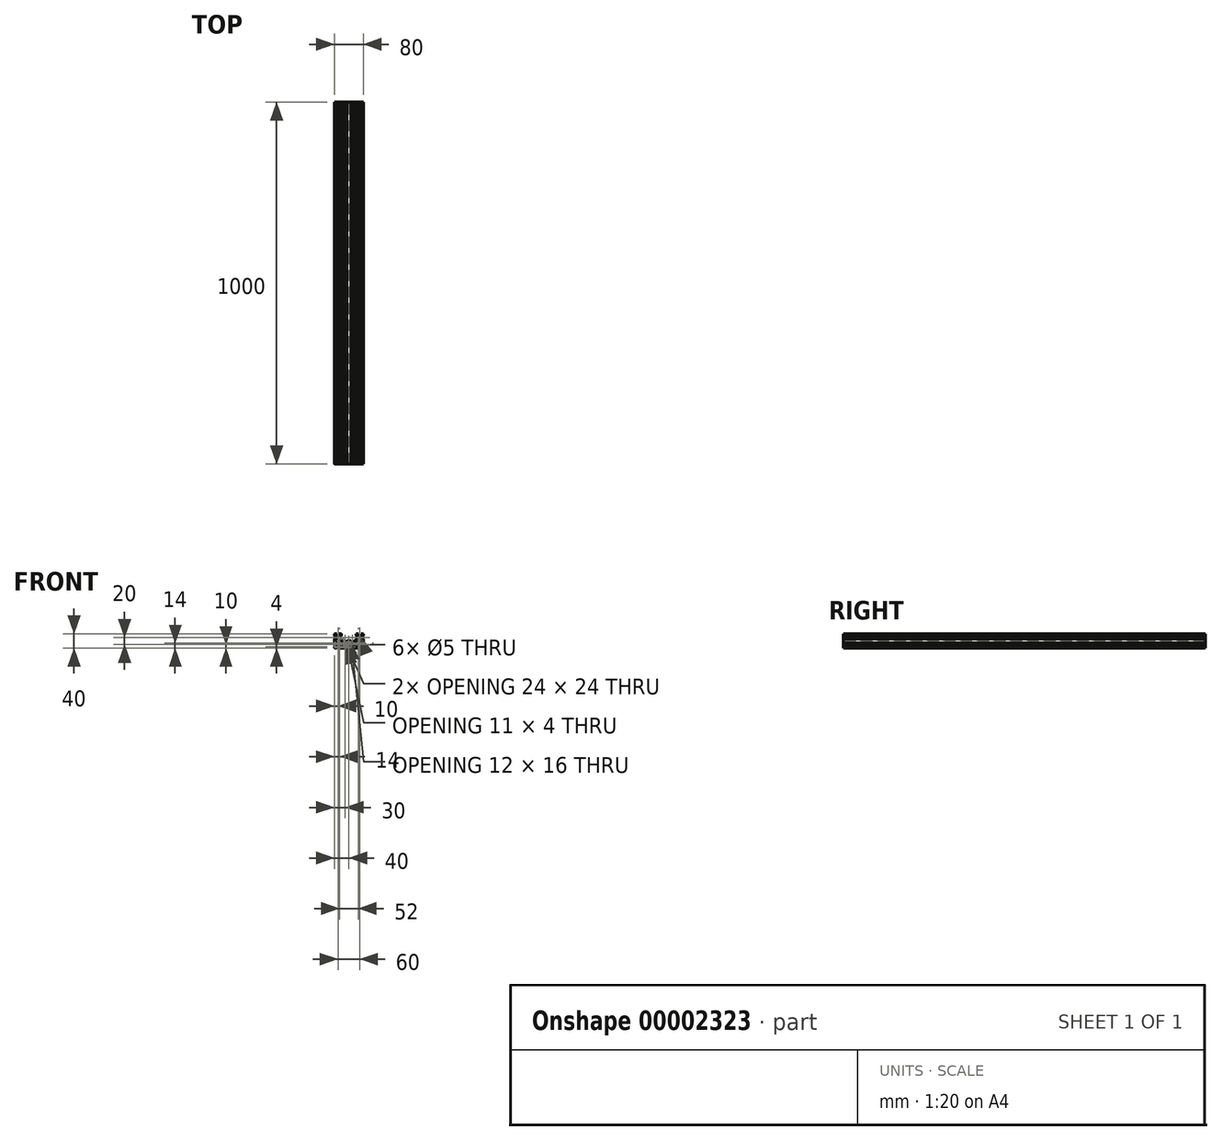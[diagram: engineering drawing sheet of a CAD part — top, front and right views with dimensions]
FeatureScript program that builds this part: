
annotation { "Feature Type Name" : "Feature", "Feature Type Description" : "" }
export const myFeature = defineFeature(function(context is Context, id is Id, definition is map)
    precondition{}
    {
        {
            var Q0;
            Q0=qCreatedBy(makeId("Front.planeOp"),FACE);
            var sketch = newSketch(context, id + "F0", { "sketchPlane" : qUnion([Q0])});
            skLineSegment(sketch, "E0", {"start": v(0, 0) * mm, "end": v(0, 40) * mm});
            skLineSegment(sketch, "E1", {"start": v(0, 40) * mm, "end": v(20, 40) * mm});
            skLineSegment(sketch, "E2", {"start": v(20, 40) * mm, "end": v(20, 20) * mm});
            skLineSegment(sketch, "E3", {"start": v(20, 20) * mm, "end": v(60, 20) * mm});
            skLineSegment(sketch, "E4", {"start": v(60, 20) * mm, "end": v(60, 40) * mm});
            skLineSegment(sketch, "E5", {"start": v(60, 40) * mm, "end": v(80, 40) * mm});
            skLineSegment(sketch, "E6", {"start": v(80, 40) * mm, "end": v(80, 0) * mm});
            skLineSegment(sketch, "E7", {"start": v(80, 0) * mm, "end": v(0, 0) * mm});
            skCircle(sketch, "E8", {"center": v(10, 30) * mm, "radius": 2.5 * mm});
            skCircle(sketch, "E9", {"center": v(10, 10) * mm, "radius": 2.5 * mm});
            skCircle(sketch, "E10", {"center": v(30, 10) * mm, "radius": 2.5 * mm});
            skCircle(sketch, "E11", {"center": v(50, 10) * mm, "radius": 2.5 * mm});
            skCircle(sketch, "E12", {"center": v(70, 10) * mm, "radius": 2.5 * mm});
            skCircle(sketch, "E13", {"center": v(70, 30) * mm, "radius": 2.5 * mm});
            skLineSegment(sketch, "E14.0", {"start": v(2, 4) * mm, "end": v(2, 15) * mm});
            skLineSegment(sketch, "E14.1", {"start": v(76, 2) * mm, "end": v(65, 2) * mm});
            skLineSegment(sketch, "E14.2", {"start": v(78, 36) * mm, "end": v(78, 25) * mm});
            skLineSegment(sketch, "E14.3", {"start": v(64, 38) * mm, "end": v(76, 38) * mm});
            skLineSegment(sketch, "E14.4", {"start": v(62, 18) * mm, "end": v(62, 23) * mm});
            skLineSegment(sketch, "E14.5", {"start": v(4, 38) * mm, "end": v(16, 38) * mm});
            skLineSegment(sketch, "E14.6", {"start": v(18, 18) * mm, "end": v(22.5, 18) * mm});
            skLineSegment(sketch, "E14.7", {"start": v(18, 36) * mm, "end": v(18, 25) * mm});
            skLineSegment(sketch, "E15.bottom", {"start": v(0, 40) * mm, "end": v(4, 40) * mm});
            skLineSegment(sketch, "E15.top", {"start": v(2, 36) * mm, "end": v(2.59, 36) * mm});
            skLineSegment(sketch, "E15.left", {"start": v(0, 40) * mm, "end": v(0, 36) * mm});
            skLineSegment(sketch, "E15.right", {"start": v(4, 38) * mm, "end": v(4, 37.41) * mm});
            skLineSegment(sketch, "E16.bottom", {"start": v(20, 40) * mm, "end": v(16, 40) * mm});
            skLineSegment(sketch, "E16.top", {"start": v(18, 36) * mm, "end": v(17.41, 36) * mm});
            skLineSegment(sketch, "E16.left", {"start": v(20, 40) * mm, "end": v(20, 36) * mm});
            skLineSegment(sketch, "E16.right", {"start": v(16, 38) * mm, "end": v(16, 37.41) * mm});
            skLineSegment(sketch, "E17.bottom", {"start": v(0, 0) * mm, "end": v(4, 0) * mm});
            skLineSegment(sketch, "E17.top", {"start": v(2, 4) * mm, "end": v(2.59, 4) * mm});
            skLineSegment(sketch, "E17.left", {"start": v(0, 0) * mm, "end": v(0, 4) * mm});
            skLineSegment(sketch, "E17.right", {"start": v(4, 2) * mm, "end": v(4, 2.59) * mm});
            skLineSegment(sketch, "E18.bottom", {"start": v(60, 40) * mm, "end": v(64, 40) * mm});
            skLineSegment(sketch, "E18.top", {"start": v(62, 36) * mm, "end": v(62.59, 36) * mm});
            skLineSegment(sketch, "E18.left", {"start": v(60, 40) * mm, "end": v(60, 36) * mm});
            skLineSegment(sketch, "E18.right", {"start": v(64, 38) * mm, "end": v(64, 37.41) * mm});
            skLineSegment(sketch, "E19.bottom", {"start": v(80, 40) * mm, "end": v(76, 40) * mm});
            skLineSegment(sketch, "E19.top", {"start": v(78, 36) * mm, "end": v(77.41, 36) * mm});
            skLineSegment(sketch, "E19.left", {"start": v(80, 40) * mm, "end": v(80, 36) * mm});
            skLineSegment(sketch, "E19.right", {"start": v(76, 38) * mm, "end": v(76, 37.41) * mm});
            skLineSegment(sketch, "E20.bottom", {"start": v(80, 0) * mm, "end": v(76, 0) * mm});
            skLineSegment(sketch, "E20.top", {"start": v(78, 4) * mm, "end": v(77.41, 4) * mm});
            skLineSegment(sketch, "E20.left", {"start": v(80, 0) * mm, "end": v(80, 4) * mm});
            skLineSegment(sketch, "E20.right", {"start": v(76, 2) * mm, "end": v(76, 2.59) * mm});
            skLineSegment(sketch, "E21.0", {"start": v(14, 32.59) * mm, "end": v(17.41, 36) * mm});
            skLineSegment(sketch, "E22.0", {"start": v(2.59, 4) * mm, "end": v(6, 7.41) * mm});
            skLineSegment(sketch, "E23.0", {"start": v(76, 2.59) * mm, "end": v(72.59, 6) * mm});
            skLineSegment(sketch, "E24.0", {"start": v(66, 32.59) * mm, "end": v(62.59, 36) * mm});
            skCircle(sketch, "E25.cCircle", {"center": v(70, 30) * mm, "radius": 4 * mm, "construction": true});
            skLineSegment(sketch, "E25.0", {"start": v(67.41, 34) * mm, "end": v(72.59, 34) * mm});
            skLineSegment(sketch, "E25.1", {"start": v(74, 32.59) * mm, "end": v(74, 27.41) * mm});
            skLineSegment(sketch, "E25.2", {"start": v(72.59, 26) * mm, "end": v(67.41, 26) * mm});
            skLineSegment(sketch, "E25.3", {"start": v(66, 27.41) * mm, "end": v(66, 32.59) * mm});
            skPoint(sketch, "E25.0.midPoint", {"position": v(70, 34) * mm});
            skCircle(sketch, "E26.cCircle", {"center": v(70, 10) * mm, "radius": 4 * mm, "construction": true});
            skLineSegment(sketch, "E26.0", {"start": v(74, 12.59) * mm, "end": v(74, 7.41) * mm});
            skLineSegment(sketch, "E26.1", {"start": v(72.59, 6) * mm, "end": v(67.41, 6) * mm});
            skLineSegment(sketch, "E26.2", {"start": v(66, 7.41) * mm, "end": v(66, 14) * mm});
            skLineSegment(sketch, "E26.3", {"start": v(66, 14) * mm, "end": v(72.59, 14) * mm});
            skPoint(sketch, "E26.0.midPoint", {"position": v(74, 10) * mm});
            skCircle(sketch, "E27.cCircle", {"center": v(10, 10) * mm, "radius": 4 * mm, "construction": true});
            skLineSegment(sketch, "E27.0", {"start": v(12.59, 6) * mm, "end": v(7.41, 6) * mm});
            skLineSegment(sketch, "E27.1", {"start": v(6, 7.41) * mm, "end": v(6, 12.59) * mm});
            skLineSegment(sketch, "E27.2", {"start": v(7.41, 14) * mm, "end": v(14, 14) * mm});
            skLineSegment(sketch, "E27.3", {"start": v(14, 14) * mm, "end": v(14, 7.41) * mm});
            skPoint(sketch, "E27.0.midPoint", {"position": v(10, 6) * mm});
            skCircle(sketch, "E28.cCircle", {"center": v(10, 30) * mm, "radius": 4 * mm, "construction": true});
            skLineSegment(sketch, "E28.0", {"start": v(6, 27.41) * mm, "end": v(6, 32.59) * mm});
            skLineSegment(sketch, "E28.1", {"start": v(7.41, 34) * mm, "end": v(12.59, 34) * mm});
            skLineSegment(sketch, "E28.2", {"start": v(14, 32.59) * mm, "end": v(14, 27.41) * mm});
            skLineSegment(sketch, "E28.3", {"start": v(12.59, 26) * mm, "end": v(7.41, 26) * mm});
            skPoint(sketch, "E28.0.midPoint", {"position": v(6, 30) * mm});
            skPoint(sketch, "E29.orphan", {"position": v(74, 6) * mm});
            skLineSegment(sketch, "E30.trimOffspring", {"start": v(77.41, 4) * mm, "end": v(74, 7.41) * mm});
            skPoint(sketch, "E31.orphan", {"position": v(74, 34) * mm});
            skPoint(sketch, "E32.orphan", {"position": v(66, 34) * mm});
            skLineSegment(sketch, "E33.trimOffspring", {"start": v(67.41, 34) * mm, "end": v(64, 37.41) * mm});
            skLineSegment(sketch, "E34.trimOffspring", {"start": v(76, 37.41) * mm, "end": v(72.59, 34) * mm});
            skLineSegment(sketch, "E35.trimOffspring", {"start": v(77.41, 36) * mm, "end": v(74, 32.59) * mm});
            skLineSegment(sketch, "E36.trimOffspring", {"start": v(7.41, 34) * mm, "end": v(4, 37.41) * mm});
            skLineSegment(sketch, "E37.trimOffspring", {"start": v(6, 32.59) * mm, "end": v(2.59, 36) * mm});
            skLineSegment(sketch, "E38.trimOffspring", {"start": v(12.59, 34) * mm, "end": v(16, 37.41) * mm});
            skPoint(sketch, "E39.orphan", {"position": v(14, 34) * mm});
            skPoint(sketch, "E40.orphan", {"position": v(6, 34) * mm});
            skPoint(sketch, "E41.orphan", {"position": v(6, 6) * mm});
            skLineSegment(sketch, "E42.trimOffspring", {"start": v(4, 2.59) * mm, "end": v(7.41, 6) * mm});
            skCircle(sketch, "E43.cCircle", {"center": v(50, 10) * mm, "radius": 4 * mm, "construction": true});
            skLineSegment(sketch, "E43.0", {"start": v(52.59, 6) * mm, "end": v(47.41, 6) * mm});
            skLineSegment(sketch, "E43.1", {"start": v(46, 7.41) * mm, "end": v(46, 12.59) * mm});
            skLineSegment(sketch, "E43.2", {"start": v(47.41, 14) * mm, "end": v(52.59, 14) * mm});
            skLineSegment(sketch, "E43.3", {"start": v(54, 12.59) * mm, "end": v(54, 7.41) * mm});
            skPoint(sketch, "E43.0.midPoint", {"position": v(50, 6) * mm});
            skCircle(sketch, "E44.cCircle", {"center": v(30, 10) * mm, "radius": 4 * mm, "construction": true});
            skLineSegment(sketch, "E44.0", {"start": v(32.59, 6) * mm, "end": v(27.41, 6) * mm});
            skLineSegment(sketch, "E44.1", {"start": v(26, 7.41) * mm, "end": v(26, 12.59) * mm});
            skLineSegment(sketch, "E44.2", {"start": v(27.41, 14) * mm, "end": v(32.59, 14) * mm});
            skLineSegment(sketch, "E44.3", {"start": v(34, 12.59) * mm, "end": v(34, 7.41) * mm});
            skPoint(sketch, "E44.0.midPoint", {"position": v(30, 6) * mm});
            skLineSegment(sketch, "E45.0", {"start": v(6, 27.41) * mm, "end": v(3.59, 25) * mm});
            skLineSegment(sketch, "E46.0", {"start": v(17, 4.41) * mm, "end": v(14, 7.41) * mm});
            skLineSegment(sketch, "E47.0", {"start": v(22.5, 16.09) * mm, "end": v(26, 12.59) * mm});
            skLineSegment(sketch, "E48.0", {"start": v(42.5, 16.09) * mm, "end": v(46, 12.59) * mm});
            skLineSegment(sketch, "E49.0", {"start": v(75.59, 17) * mm, "end": v(72.59, 14) * mm});
            skLineSegment(sketch, "E50.0", {"start": v(72.59, 26) * mm, "end": v(75.59, 23) * mm});
            skLineSegment(sketch, "E51.0", {"start": v(14, 27.41) * mm, "end": v(16.41, 25) * mm});
            skLineSegment(sketch, "E52.0", {"start": v(37.5, 16.09) * mm, "end": v(34, 12.59) * mm});
            skLineSegment(sketch, "E53.0", {"start": v(57.5, 16.09) * mm, "end": v(54, 12.59) * mm});
            skLineSegment(sketch, "E54.0", {"start": v(44.5, 16.91) * mm, "end": v(47.41, 14) * mm});
            skLineSegment(sketch, "E55.0", {"start": v(76.41, 15) * mm, "end": v(74, 12.59) * mm});
            skLineSegment(sketch, "E56", {"start": v(2, 25) * mm, "end": v(3.59, 25) * mm});
            skLineSegment(sketch, "E57", {"start": v(78, 23) * mm, "end": v(75.59, 23) * mm});
            skPoint(sketch, "E58.orphan", {"position": v(6, 26) * mm});
            skLineSegment(sketch, "E59.trimOffspring", {"start": v(7.41, 26) * mm, "end": v(4.41, 23) * mm});
            skLineSegment(sketch, "E60.trimOffspring", {"start": v(12.59, 26) * mm, "end": v(15.59, 23) * mm});
            skPoint(sketch, "E61.orphan", {"position": v(14, 26) * mm});
            skLineSegment(sketch, "E62.trimOffspring", {"start": v(16.41, 25) * mm, "end": v(18, 25) * mm});
            skLineSegment(sketch, "E63.trimOffspring", {"start": v(4.41, 23) * mm, "end": v(2, 23) * mm});
            skLineSegment(sketch, "E64.trimOffspring", {"start": v(62, 25) * mm, "end": v(63.59, 25) * mm});
            skLineSegment(sketch, "E65.trimOffspring", {"start": v(18, 23) * mm, "end": v(18, 18) * mm});
            skLineSegment(sketch, "E66.trimOffspring", {"start": v(18, 23) * mm, "end": v(15.59, 23) * mm});
            skLineSegment(sketch, "E67.trimOffspring", {"start": v(2, 25) * mm, "end": v(2, 36) * mm});
            skLineSegment(sketch, "E68.trimOffspring", {"start": v(66, 27.41) * mm, "end": v(63.59, 25) * mm});
            skLineSegment(sketch, "E69.trimOffspring", {"start": v(67.41, 26) * mm, "end": v(64.41, 23) * mm});
            skPoint(sketch, "E70.orphan", {"position": v(66, 26) * mm});
            skPoint(sketch, "E71.orphan", {"position": v(74, 26) * mm});
            skLineSegment(sketch, "E72.trimOffspring", {"start": v(74, 27.41) * mm, "end": v(76.41, 25) * mm});
            skLineSegment(sketch, "E73.trimOffspring", {"start": v(76.41, 25) * mm, "end": v(78, 25) * mm});
            skLineSegment(sketch, "E74.trimOffspring", {"start": v(62, 25) * mm, "end": v(62, 36) * mm});
            skLineSegment(sketch, "E75.trimOffspring", {"start": v(64.41, 23) * mm, "end": v(62, 23) * mm});
            skLineSegment(sketch, "E76.trimOffspring", {"start": v(78, 23) * mm, "end": v(78, 17) * mm});
            skLineSegment(sketch, "E77", {"start": v(2, 17) * mm, "end": v(4.41, 17) * mm});
            skLineSegment(sketch, "E78", {"start": v(2, 15) * mm, "end": v(3.59, 15) * mm});
            skLineSegment(sketch, "E79.trimOffspring", {"start": v(75.59, 17) * mm, "end": v(78, 17) * mm});
            skLineSegment(sketch, "E80.trimOffspring", {"start": v(76.41, 15) * mm, "end": v(78, 15) * mm});
            skLineSegment(sketch, "E81.trimOffspring", {"start": v(2, 17) * mm, "end": v(2, 23) * mm});
            skPoint(sketch, "E82.orphan", {"position": v(6, 14) * mm});
            skLineSegment(sketch, "E83.trimOffspring", {"start": v(7.41, 14) * mm, "end": v(4.41, 17) * mm});
            skLineSegment(sketch, "E84.trimOffspring", {"start": v(6, 12.59) * mm, "end": v(3.59, 15) * mm});
            skLineSegment(sketch, "E85.trimOffspring", {"start": v(78, 15) * mm, "end": v(78, 4) * mm});
            skPoint(sketch, "E86.orphan", {"position": v(74, 14) * mm});
            skLineSegment(sketch, "E87.trimOffspring", {"start": v(67.41, 6) * mm, "end": v(65, 3.59) * mm});
            skLineSegment(sketch, "E88.trimOffspring", {"start": v(66, 7.41) * mm, "end": v(63, 4.41) * mm});
            skPoint(sketch, "E89.orphan", {"position": v(14, 6) * mm});
            skLineSegment(sketch, "E90.trimOffspring", {"start": v(63, 4.41) * mm, "end": v(63, 2) * mm});
            skLineSegment(sketch, "E91.trimOffspring", {"start": v(15, 3.59) * mm, "end": v(12.59, 6) * mm});
            skLineSegment(sketch, "E92.trimOffspring", {"start": v(15, 2) * mm, "end": v(4, 2) * mm});
            skLineSegment(sketch, "E93.trimOffspring", {"start": v(17, 2) * mm, "end": v(17, 4.41) * mm});
            skLineSegment(sketch, "E94.trimOffspring", {"start": v(15, 3.59) * mm, "end": v(15, 2) * mm});
            skLineSegment(sketch, "E95.trimOffspring", {"start": v(65, 3.59) * mm, "end": v(65, 2) * mm});
            skPoint(sketch, "E96.orphan", {"position": v(66, 6) * mm});
            skLineSegment(sketch, "E97.trimOffspring", {"start": v(63, 2) * mm, "end": v(57.5, 2) * mm});
            skLineSegment(sketch, "E98.0", {"start": v(37.5, 2) * mm, "end": v(37.5, 3.91) * mm});
            skLineSegment(sketch, "E99.0", {"start": v(22.5, 2) * mm, "end": v(22.5, 3.91) * mm});
            skLineSegment(sketch, "E100.0", {"start": v(57.5, 2) * mm, "end": v(57.5, 3.91) * mm});
            skLineSegment(sketch, "E101.0", {"start": v(42.5, 2) * mm, "end": v(42.5, 3.91) * mm});
            skLineSegment(sketch, "E102.0", {"start": v(24.5, 2) * mm, "end": v(24.5, 3.09) * mm});
            skLineSegment(sketch, "E103.0", {"start": v(35.5, 2) * mm, "end": v(35.5, 3.09) * mm});
            skLineSegment(sketch, "E104.0", {"start": v(44.5, 2) * mm, "end": v(44.5, 3.09) * mm});
            skLineSegment(sketch, "E105.0", {"start": v(55.5, 2) * mm, "end": v(55.5, 3.09) * mm});
            skLineSegment(sketch, "E106.trimOffspring", {"start": v(24.5, 16.91) * mm, "end": v(27.41, 14) * mm});
            skLineSegment(sketch, "E107.trimOffspring", {"start": v(24.5, 18) * mm, "end": v(35.5, 18) * mm});
            skLineSegment(sketch, "E108.trimOffspring", {"start": v(24.5, 16.91) * mm, "end": v(24.5, 18) * mm});
            skLineSegment(sketch, "E109.trimOffspring", {"start": v(22.5, 16.09) * mm, "end": v(22.5, 18) * mm});
            skLineSegment(sketch, "E110.trimOffspring", {"start": v(22.5, 2) * mm, "end": v(17, 2) * mm});
            skLineSegment(sketch, "E111.trimOffspring", {"start": v(35.5, 16.91) * mm, "end": v(32.59, 14) * mm});
            skLineSegment(sketch, "E112.trimOffspring", {"start": v(35.5, 16.91) * mm, "end": v(35.5, 18) * mm});
            skLineSegment(sketch, "E113.trimOffspring", {"start": v(37.5, 18) * mm, "end": v(42.5, 18) * mm});
            skLineSegment(sketch, "E114.trimOffspring", {"start": v(37.5, 16.09) * mm, "end": v(37.5, 18) * mm});
            skLineSegment(sketch, "E115.trimOffspring", {"start": v(35.5, 2) * mm, "end": v(24.5, 2) * mm});
            skPoint(sketch, "E116.orphan", {"position": v(26, 14) * mm});
            skPoint(sketch, "E117.orphan", {"position": v(34, 14) * mm});
            skPoint(sketch, "E118.orphan", {"position": v(34, 6) * mm});
            skPoint(sketch, "E119.orphan", {"position": v(26, 6) * mm});
            skLineSegment(sketch, "E120.trimOffspring", {"start": v(34, 7.41) * mm, "end": v(37.5, 3.91) * mm});
            skLineSegment(sketch, "E121.trimOffspring", {"start": v(32.59, 6) * mm, "end": v(35.5, 3.09) * mm});
            skLineSegment(sketch, "E122.trimOffspring", {"start": v(27.41, 6) * mm, "end": v(24.5, 3.09) * mm});
            skLineSegment(sketch, "E123.trimOffspring", {"start": v(26, 7.41) * mm, "end": v(22.5, 3.91) * mm});
            skLineSegment(sketch, "E124.trimOffspring", {"start": v(44.5, 18) * mm, "end": v(55.5, 18) * mm});
            skLineSegment(sketch, "E125.trimOffspring", {"start": v(42.5, 16.09) * mm, "end": v(42.5, 18) * mm});
            skLineSegment(sketch, "E126.trimOffspring", {"start": v(44.5, 16.91) * mm, "end": v(44.5, 18) * mm});
            skLineSegment(sketch, "E127.trimOffspring", {"start": v(42.5, 2) * mm, "end": v(37.5, 2) * mm});
            skPoint(sketch, "E128.orphan", {"position": v(46, 6) * mm});
            skPoint(sketch, "E129.orphan", {"position": v(46, 14) * mm});
            skLineSegment(sketch, "E130.trimOffspring", {"start": v(46, 7.41) * mm, "end": v(42.5, 3.91) * mm});
            skLineSegment(sketch, "E131.trimOffspring", {"start": v(47.97, 6.55) * mm, "end": v(44.5, 3.09) * mm});
            skPoint(sketch, "E132.orphan", {"position": v(54, 6) * mm});
            skPoint(sketch, "E133.orphan", {"position": v(54, 14) * mm});
            skLineSegment(sketch, "E134.trimOffspring", {"start": v(54, 7.41) * mm, "end": v(57.5, 3.91) * mm});
            skLineSegment(sketch, "E135.trimOffspring", {"start": v(52.59, 6) * mm, "end": v(55.5, 3.09) * mm});
            skLineSegment(sketch, "E136.trimOffspring", {"start": v(55.5, 16.91) * mm, "end": v(52.59, 14) * mm});
            skLineSegment(sketch, "E137.trimOffspring", {"start": v(57.5, 18) * mm, "end": v(62, 18) * mm});
            skLineSegment(sketch, "E138.trimOffspring", {"start": v(55.5, 16.91) * mm, "end": v(55.5, 18) * mm});
            skLineSegment(sketch, "E139.trimOffspring", {"start": v(57.5, 16.09) * mm, "end": v(57.5, 18) * mm});
            skLineSegment(sketch, "E140.trimOffspring", {"start": v(55.5, 2) * mm, "end": v(44.5, 2) * mm});
            skSolve(sketch);
        }
        {
            var Q0;
            Q0 = qSketchRegion(id + "F0", true);
            extrude(context, id + "F1", {"entities" : qUnion([Q0]), "depth" : 1000 * mm});
        }
        {
            var Q0;
            Q0=makeQuery(id+"F1.opExtrude","CAP_FACE",FACE,{"disambiguationData":[OSD([sQuery(id+"F0.wireOp",EDGE,"E0"),sQuery(id+"F0.wireOp",EDGE,"E2"),sQuery(id+"F0.wireOp",EDGE,"E3"),sQuery(id+"F0.wireOp",EDGE,"E8"),sQuery(id+"F0.wireOp",EDGE,"E9"),sQuery(id+"F0.wireOp",EDGE,"E10"),sQuery(id+"F0.wireOp",EDGE,"E11"),sQuery(id+"F0.wireOp",EDGE,"E12"),sQuery(id+"F0.wireOp",EDGE,"E13"),sQuery(id+"F0.wireOp",EDGE,"E14.0"),sQuery(id+"F0.wireOp",EDGE,"E14.1"),sQuery(id+"F0.wireOp",EDGE,"E14.2"),sQuery(id+"F0.wireOp",EDGE,"E14.3"),sQuery(id+"F0.wireOp",EDGE,"E14.4"),sQuery(id+"F0.wireOp",EDGE,"E14.5"),sQuery(id+"F0.wireOp",EDGE,"E14.6"),sQuery(id+"F0.wireOp",EDGE,"E14.7"),sQuery(id+"F0.wireOp",EDGE,"E15.top"),sQuery(id+"F0.wireOp",EDGE,"E15.right"),sQuery(id+"F0.wireOp",EDGE,"E16.bottom"),sQuery(id+"F0.wireOp",EDGE,"E16.top"),sQuery(id+"F0.wireOp",EDGE,"E16.right"),sQuery(id+"F0.wireOp",EDGE,"E17.bottom"),sQuery(id+"F0.wireOp",EDGE,"E17.top"),sQuery(id+"F0.wireOp",EDGE,"E17.right"),sQuery(id+"F0.wireOp",EDGE,"E18.top"),sQuery(id+"F0.wireOp",EDGE,"E18.left"),sQuery(id+"F0.wireOp",EDGE,"E18.right"),sQuery(id+"F0.wireOp",EDGE,"E19.bottom"),sQuery(id+"F0.wireOp",EDGE,"E19.top"),sQuery(id+"F0.wireOp",EDGE,"E19.right"),sQuery(id+"F0.wireOp",EDGE,"E20.top"),sQuery(id+"F0.wireOp",EDGE,"E20.left"),sQuery(id+"F0.wireOp",EDGE,"E20.right"),sQuery(id+"F0.wireOp",EDGE,"E21.0"),sQuery(id+"F0.wireOp",EDGE,"E22.0"),sQuery(id+"F0.wireOp",EDGE,"E23.0"),sQuery(id+"F0.wireOp",EDGE,"E24.0"),sQuery(id+"F0.wireOp",EDGE,"E25.0"),sQuery(id+"F0.wireOp",EDGE,"E25.1"),sQuery(id+"F0.wireOp",EDGE,"E25.2"),sQuery(id+"F0.wireOp",EDGE,"E25.3"),sQuery(id+"F0.wireOp",EDGE,"E26.0"),sQuery(id+"F0.wireOp",EDGE,"E26.1"),sQuery(id+"F0.wireOp",EDGE,"E26.2"),sQuery(id+"F0.wireOp",EDGE,"E26.3"),sQuery(id+"F0.wireOp",EDGE,"E27.0"),sQuery(id+"F0.wireOp",EDGE,"E27.1"),sQuery(id+"F0.wireOp",EDGE,"E27.2"),sQuery(id+"F0.wireOp",EDGE,"E27.3"),sQuery(id+"F0.wireOp",EDGE,"E28.0"),sQuery(id+"F0.wireOp",EDGE,"E28.1"),sQuery(id+"F0.wireOp",EDGE,"E28.2"),sQuery(id+"F0.wireOp",EDGE,"E28.3"),sQuery(id+"F0.wireOp",EDGE,"E30.trimOffspring"),sQuery(id+"F0.wireOp",EDGE,"E33.trimOffspring"),sQuery(id+"F0.wireOp",EDGE,"E34.trimOffspring"),sQuery(id+"F0.wireOp",EDGE,"E35.trimOffspring"),sQuery(id+"F0.wireOp",EDGE,"E36.trimOffspring"),sQuery(id+"F0.wireOp",EDGE,"E37.trimOffspring"),sQuery(id+"F0.wireOp",EDGE,"E38.trimOffspring"),sQuery(id+"F0.wireOp",EDGE,"E42.trimOffspring"),sQuery(id+"F0.wireOp",EDGE,"E43.0"),sQuery(id+"F0.wireOp",EDGE,"E43.1"),sQuery(id+"F0.wireOp",EDGE,"E43.2"),sQuery(id+"F0.wireOp",EDGE,"E43.3"),sQuery(id+"F0.wireOp",EDGE,"E44.0"),sQuery(id+"F0.wireOp",EDGE,"E44.1"),sQuery(id+"F0.wireOp",EDGE,"E44.2"),sQuery(id+"F0.wireOp",EDGE,"E44.3"),sQuery(id+"F0.wireOp",EDGE,"E45.0"),sQuery(id+"F0.wireOp",EDGE,"E46.0"),sQuery(id+"F0.wireOp",EDGE,"E47.0"),sQuery(id+"F0.wireOp",EDGE,"E48.0"),sQuery(id+"F0.wireOp",EDGE,"E49.0"),sQuery(id+"F0.wireOp",EDGE,"E50.0"),sQuery(id+"F0.wireOp",EDGE,"E51.0"),sQuery(id+"F0.wireOp",EDGE,"E52.0"),sQuery(id+"F0.wireOp",EDGE,"E53.0"),sQuery(id+"F0.wireOp",EDGE,"E54.0"),sQuery(id+"F0.wireOp",EDGE,"E55.0"),sQuery(id+"F0.wireOp",EDGE,"E56"),sQuery(id+"F0.wireOp",EDGE,"E57"),sQuery(id+"F0.wireOp",EDGE,"E59.trimOffspring"),sQuery(id+"F0.wireOp",EDGE,"E60.trimOffspring"),sQuery(id+"F0.wireOp",EDGE,"E62.trimOffspring"),sQuery(id+"F0.wireOp",EDGE,"E63.trimOffspring"),sQuery(id+"F0.wireOp",EDGE,"E64.trimOffspring"),sQuery(id+"F0.wireOp",EDGE,"E65.trimOffspring"),sQuery(id+"F0.wireOp",EDGE,"E66.trimOffspring"),sQuery(id+"F0.wireOp",EDGE,"E67.trimOffspring"),sQuery(id+"F0.wireOp",EDGE,"E68.trimOffspring"),sQuery(id+"F0.wireOp",EDGE,"E69.trimOffspring"),sQuery(id+"F0.wireOp",EDGE,"E72.trimOffspring"),sQuery(id+"F0.wireOp",EDGE,"E73.trimOffspring"),sQuery(id+"F0.wireOp",EDGE,"E74.trimOffspring"),sQuery(id+"F0.wireOp",EDGE,"E75.trimOffspring"),sQuery(id+"F0.wireOp",EDGE,"E76.trimOffspring"),sQuery(id+"F0.wireOp",EDGE,"E77"),sQuery(id+"F0.wireOp",EDGE,"E78"),sQuery(id+"F0.wireOp",EDGE,"E79.trimOffspring"),sQuery(id+"F0.wireOp",EDGE,"E80.trimOffspring"),sQuery(id+"F0.wireOp",EDGE,"E81.trimOffspring"),sQuery(id+"F0.wireOp",EDGE,"E83.trimOffspring"),sQuery(id+"F0.wireOp",EDGE,"E84.trimOffspring"),sQuery(id+"F0.wireOp",EDGE,"E85.trimOffspring"),sQuery(id+"F0.wireOp",EDGE,"E87.trimOffspring"),sQuery(id+"F0.wireOp",EDGE,"E88.trimOffspring"),sQuery(id+"F0.wireOp",EDGE,"E90.trimOffspring"),sQuery(id+"F0.wireOp",EDGE,"E91.trimOffspring"),sQuery(id+"F0.wireOp",EDGE,"E92.trimOffspring"),sQuery(id+"F0.wireOp",EDGE,"E93.trimOffspring"),sQuery(id+"F0.wireOp",EDGE,"E94.trimOffspring"),sQuery(id+"F0.wireOp",EDGE,"E95.trimOffspring"),sQuery(id+"F0.wireOp",EDGE,"E97.trimOffspring"),sQuery(id+"F0.wireOp",EDGE,"E98.0"),sQuery(id+"F0.wireOp",EDGE,"E99.0"),sQuery(id+"F0.wireOp",EDGE,"E100.0"),sQuery(id+"F0.wireOp",EDGE,"E101.0"),sQuery(id+"F0.wireOp",EDGE,"E102.0"),sQuery(id+"F0.wireOp",EDGE,"E103.0"),sQuery(id+"F0.wireOp",EDGE,"E104.0"),sQuery(id+"F0.wireOp",EDGE,"E105.0"),sQuery(id+"F0.wireOp",EDGE,"E106.trimOffspring"),sQuery(id+"F0.wireOp",EDGE,"E107.trimOffspring"),sQuery(id+"F0.wireOp",EDGE,"E108.trimOffspring"),sQuery(id+"F0.wireOp",EDGE,"E109.trimOffspring"),sQuery(id+"F0.wireOp",EDGE,"E110.trimOffspring"),sQuery(id+"F0.wireOp",EDGE,"E111.trimOffspring"),sQuery(id+"F0.wireOp",EDGE,"E112.trimOffspring"),sQuery(id+"F0.wireOp",EDGE,"E113.trimOffspring"),sQuery(id+"F0.wireOp",EDGE,"E114.trimOffspring"),sQuery(id+"F0.wireOp",EDGE,"E115.trimOffspring"),sQuery(id+"F0.wireOp",EDGE,"E120.trimOffspring"),sQuery(id+"F0.wireOp",EDGE,"E121.trimOffspring"),sQuery(id+"F0.wireOp",EDGE,"E122.trimOffspring"),sQuery(id+"F0.wireOp",EDGE,"E123.trimOffspring"),sQuery(id+"F0.wireOp",EDGE,"E124.trimOffspring"),sQuery(id+"F0.wireOp",EDGE,"E125.trimOffspring"),sQuery(id+"F0.wireOp",EDGE,"E126.trimOffspring"),sQuery(id+"F0.wireOp",EDGE,"E127.trimOffspring"),sQuery(id+"F0.wireOp",EDGE,"E130.trimOffspring"),sQuery(id+"F0.wireOp",EDGE,"E131.trimOffspring"),sQuery(id+"F0.wireOp",EDGE,"E134.trimOffspring"),sQuery(id+"F0.wireOp",EDGE,"E135.trimOffspring"),sQuery(id+"F0.wireOp",EDGE,"E136.trimOffspring"),sQuery(id+"F0.wireOp",EDGE,"E137.trimOffspring"),sQuery(id+"F0.wireOp",EDGE,"E138.trimOffspring"),sQuery(id+"F0.wireOp",EDGE,"E139.trimOffspring"),sQuery(id+"F0.wireOp",EDGE,"E140.trimOffspring")])],"isStart":false});
            var sketch = newSketch(context, id + "F2", { "sketchPlane" : qUnion([Q0])});
            skPoint(sketch, "E141.orphan", {"position": v(10, 10) * mm});
            skLineSegment(sketch, "E142", {"start": v(30, 10) * mm, "end": v(30, 22.67) * mm});
            skLineSegment(sketch, "E143", {"start": v(50, 10) * mm, "end": v(50, 23.9) * mm});
            skLineSegment(sketch, "E144", {"start": v(70, 10) * mm, "end": v(70, 43) * mm});
            skLineSegment(sketch, "E145", {"start": v(25.5, 20) * mm, "end": v(26.5, 19) * mm});
            skLineSegment(sketch, "E146", {"start": v(26.5, 19) * mm, "end": v(26.5, 17.05) * mm});
            skLineSegment(sketch, "E147", {"start": v(26.5, 17.05) * mm, "end": v(33.5, 17.05) * mm});
            skLineSegment(sketch, "E148", {"start": v(33.5, 17.05) * mm, "end": v(33.5, 19) * mm});
            skLineSegment(sketch, "E149", {"start": v(33.5, 19) * mm, "end": v(34.5, 20) * mm});
            skLineSegment(sketch, "E150", {"start": v(34.5, 20) * mm, "end": v(25.5, 20) * mm});
            skLineSegment(sketch, "E151", {"start": v(25.5, 0) * mm, "end": v(34.5, 0) * mm});
            skLineSegment(sketch, "E152", {"start": v(34.5, 0) * mm, "end": v(33.5, 1) * mm});
            skLineSegment(sketch, "E153", {"start": v(33.5, 1) * mm, "end": v(33.5, 3.85) * mm});
            skLineSegment(sketch, "E154", {"start": v(33.5, 3.85) * mm, "end": v(26.5, 3.85) * mm});
            skLineSegment(sketch, "E155", {"start": v(26.5, 3.85) * mm, "end": v(26.5, 1) * mm});
            skLineSegment(sketch, "E156", {"start": v(26.5, 1) * mm, "end": v(25.5, 0) * mm});
            skLineSegment(sketch, "E157", {"start": v(45.5, 20) * mm, "end": v(46.5, 19) * mm});
            skLineSegment(sketch, "E158", {"start": v(46.5, 19) * mm, "end": v(46.5, 16.95) * mm});
            skLineSegment(sketch, "E159", {"start": v(46.5, 16.95) * mm, "end": v(53.5, 16.95) * mm});
            skLineSegment(sketch, "E160", {"start": v(53.5, 16.95) * mm, "end": v(53.5, 19) * mm});
            skLineSegment(sketch, "E161", {"start": v(53.5, 19) * mm, "end": v(54.5, 20) * mm});
            skLineSegment(sketch, "E162", {"start": v(54.5, 20) * mm, "end": v(45.5, 20) * mm});
            skLineSegment(sketch, "E163", {"start": v(45.5, 0) * mm, "end": v(46.5, 1) * mm});
            skLineSegment(sketch, "E164", {"start": v(46.5, 1) * mm, "end": v(46.5, 2.96) * mm});
            skLineSegment(sketch, "E165", {"start": v(46.5, 2.96) * mm, "end": v(53.5, 2.96) * mm});
            skLineSegment(sketch, "E166", {"start": v(53.5, 2.96) * mm, "end": v(53.5, 1) * mm});
            skLineSegment(sketch, "E167", {"start": v(53.5, 1) * mm, "end": v(54.5, 0) * mm});
            skLineSegment(sketch, "E168", {"start": v(54.5, 0) * mm, "end": v(45.5, 0) * mm});
            skLineSegment(sketch, "E169", {"start": v(65.5, 40) * mm, "end": v(66.5, 39) * mm});
            skLineSegment(sketch, "E170", {"start": v(66.5, 39) * mm, "end": v(66.5, 36.05) * mm});
            skLineSegment(sketch, "E171", {"start": v(66.5, 36.05) * mm, "end": v(73.5, 36.05) * mm});
            skLineSegment(sketch, "E172", {"start": v(73.5, 36.05) * mm, "end": v(73.5, 39) * mm});
            skLineSegment(sketch, "E173", {"start": v(73.5, 39) * mm, "end": v(74.5, 40) * mm});
            skLineSegment(sketch, "E174", {"start": v(74.5, 40) * mm, "end": v(65.5, 40) * mm});
            skLineSegment(sketch, "E175", {"start": v(65.5, 0) * mm, "end": v(66.5, 1) * mm});
            skLineSegment(sketch, "E176", {"start": v(66.5, 1) * mm, "end": v(66.5, 3.5) * mm});
            skLineSegment(sketch, "E177", {"start": v(66.5, 3.5) * mm, "end": v(73.5, 3.5) * mm});
            skLineSegment(sketch, "E178", {"start": v(73.5, 3.5) * mm, "end": v(73.5, 1) * mm});
            skLineSegment(sketch, "E179", {"start": v(73.5, 1) * mm, "end": v(74.5, 0) * mm});
            skLineSegment(sketch, "E180", {"start": v(74.5, 0) * mm, "end": v(65.5, 0) * mm});
            skLineSegment(sketch, "E181", {"start": v(10, 10) * mm, "end": v(-11.8, 10) * mm});
            skLineSegment(sketch, "E182", {"start": v(0, 5.5) * mm, "end": v(1, 6.5) * mm});
            skLineSegment(sketch, "E183", {"start": v(1, 6.5) * mm, "end": v(4, 6.5) * mm});
            skLineSegment(sketch, "E184", {"start": v(4, 6.5) * mm, "end": v(4, 13.5) * mm});
            skLineSegment(sketch, "E185", {"start": v(4, 13.5) * mm, "end": v(1, 13.5) * mm});
            skLineSegment(sketch, "E186", {"start": v(1, 13.5) * mm, "end": v(0, 14.5) * mm});
            skLineSegment(sketch, "E187", {"start": v(0, 14.5) * mm, "end": v(0, 5.5) * mm});
            skLineSegment(sketch, "E188", {"start": v(-15.93, 20) * mm, "end": v(98.8, 20) * mm});
            skLineSegment(sketch, "E189.0.MirrorCS", {"start": v(4, 26.5) * mm, "end": v(1, 26.5) * mm});
            skLineSegment(sketch, "E190.0.MirrorCS", {"start": v(4, 33.5) * mm, "end": v(4, 26.5) * mm});
            skLineSegment(sketch, "E191.0.MirrorCS", {"start": v(1, 33.5) * mm, "end": v(4, 33.5) * mm});
            skLineSegment(sketch, "E192.0.MirrorCS", {"start": v(0, 34.5) * mm, "end": v(1, 33.5) * mm});
            skLineSegment(sketch, "E193.0.MirrorCS", {"start": v(0, 25.5) * mm, "end": v(0, 34.5) * mm});
            skLineSegment(sketch, "E194.0.MirrorCS", {"start": v(1, 26.5) * mm, "end": v(0, 25.5) * mm});
            skLineSegment(sketch, "E195", {"start": v(40, 43.94) * mm, "end": v(40, -12.41) * mm});
            skLineSegment(sketch, "E196", {"start": v(10, 45.71) * mm, "end": v(10, -12.24) * mm});
            skLineSegment(sketch, "E197.0.MirrorCS", {"start": v(16, 33.5) * mm, "end": v(16, 26.5) * mm});
            skLineSegment(sketch, "E198.0.MirrorCS", {"start": v(16, 26.5) * mm, "end": v(19, 26.5) * mm});
            skLineSegment(sketch, "E199.0.MirrorCS", {"start": v(19, 33.5) * mm, "end": v(16, 33.5) * mm});
            skLineSegment(sketch, "E200.0.MirrorCS", {"start": v(20, 25.5) * mm, "end": v(20, 34.5) * mm});
            skLineSegment(sketch, "E201.0.MirrorCS", {"start": v(20, 34.5) * mm, "end": v(19, 33.5) * mm});
            skLineSegment(sketch, "E202.0.MirrorCS", {"start": v(19, 26.5) * mm, "end": v(20, 25.5) * mm});
            skLineSegment(sketch, "E203.0.MirrorCS", {"start": v(60, 34.5) * mm, "end": v(61, 33.5) * mm});
            skLineSegment(sketch, "E203.1.MirrorCS", {"start": v(80, 34.5) * mm, "end": v(79, 33.5) * mm});
            skLineSegment(sketch, "E203.2.MirrorCS", {"start": v(61, 26.5) * mm, "end": v(60, 25.5) * mm});
            skLineSegment(sketch, "E203.3.MirrorCS", {"start": v(79, 26.5) * mm, "end": v(80, 25.5) * mm});
            skLineSegment(sketch, "E203.4.MirrorCS", {"start": v(80, 25.5) * mm, "end": v(80, 34.5) * mm});
            skLineSegment(sketch, "E203.5.MirrorCS", {"start": v(76, 33.5) * mm, "end": v(76, 26.5) * mm});
            skLineSegment(sketch, "E203.6.MirrorCS", {"start": v(79, 33.5) * mm, "end": v(76, 33.5) * mm});
            skLineSegment(sketch, "E203.7.MirrorCS", {"start": v(76, 26.5) * mm, "end": v(79, 26.5) * mm});
            skLineSegment(sketch, "E203.8.MirrorCS", {"start": v(64, 33.5) * mm, "end": v(64, 26.5) * mm});
            skLineSegment(sketch, "E203.9.MirrorCS", {"start": v(60, 25.5) * mm, "end": v(60, 34.5) * mm});
            skLineSegment(sketch, "E203.10.MirrorCS", {"start": v(61, 33.5) * mm, "end": v(64, 33.5) * mm});
            skLineSegment(sketch, "E203.11.MirrorCS", {"start": v(64, 26.5) * mm, "end": v(61, 26.5) * mm});
            skLineSegment(sketch, "E204.0.MirrorCS", {"start": v(79, 13.5) * mm, "end": v(80, 14.5) * mm});
            skLineSegment(sketch, "E204.1.MirrorCS", {"start": v(80, 5.5) * mm, "end": v(79, 6.5) * mm});
            skLineSegment(sketch, "E204.2.MirrorCS", {"start": v(76, 13.5) * mm, "end": v(79, 13.5) * mm});
            skLineSegment(sketch, "E204.3.MirrorCS", {"start": v(80, 14.5) * mm, "end": v(80, 5.5) * mm});
            skLineSegment(sketch, "E204.4.MirrorCS", {"start": v(79, 6.5) * mm, "end": v(76, 6.5) * mm});
            skLineSegment(sketch, "E204.5.MirrorCS", {"start": v(76, 6.5) * mm, "end": v(76, 13.5) * mm});
            skLineSegment(sketch, "E205.0.MirrorCS", {"start": v(6.5, 39) * mm, "end": v(5.5, 40) * mm});
            skLineSegment(sketch, "E205.1.MirrorCS", {"start": v(14.5, 40) * mm, "end": v(13.5, 39) * mm});
            skLineSegment(sketch, "E205.2.MirrorCS", {"start": v(13.5, 39) * mm, "end": v(13.5, 36.05) * mm});
            skLineSegment(sketch, "E205.3.MirrorCS", {"start": v(13.5, 36.05) * mm, "end": v(6.5, 36.05) * mm});
            skLineSegment(sketch, "E205.4.MirrorCS", {"start": v(6.5, 36.05) * mm, "end": v(6.5, 39) * mm});
            skLineSegment(sketch, "E205.5.MirrorCS", {"start": v(5.5, 40) * mm, "end": v(14.5, 40) * mm});
            skLineSegment(sketch, "E206.0.MirrorCS", {"start": v(14.5, 0) * mm, "end": v(13.5, 1) * mm});
            skLineSegment(sketch, "E206.1.MirrorCS", {"start": v(13.5, 1) * mm, "end": v(13.5, 3.5) * mm});
            skLineSegment(sketch, "E206.2.MirrorCS", {"start": v(13.5, 3.5) * mm, "end": v(6.5, 3.5) * mm});
            skLineSegment(sketch, "E206.3.MirrorCS", {"start": v(6.5, 1) * mm, "end": v(5.5, 0) * mm});
            skLineSegment(sketch, "E206.4.MirrorCS", {"start": v(5.5, 0) * mm, "end": v(14.5, 0) * mm});
            skLineSegment(sketch, "E206.5.MirrorCS", {"start": v(6.5, 3.5) * mm, "end": v(6.5, 1) * mm});
            skSolve(sketch);
        }
        {
            var Q0;
            {var subQ8=sQuery(id+"F2.wireOp",EDGE,"E154");var subQ16=sQuery(id+"F2.wireOp",EDGE,"E163");var subQ17=sQuery(id+"F2.wireOp",EDGE,"E165");var subQ25=sQuery(id+"F2.wireOp",EDGE,"E175");var subQ26=sQuery(id+"F2.wireOp",EDGE,"E177");var subQ33=sQuery(id+"F2.wireOp",EDGE,"E190.0.MirrorCS");var subQ35=sQuery(id+"F2.wireOp",EDGE,"E192.0.MirrorCS");var subQ42=sQuery(id+"F2.wireOp",EDGE,"E197.0.MirrorCS");var subQ52=sQuery(id+"F2.wireOp",EDGE,"E203.0.MirrorCS");var subQ60=sQuery(id+"F2.wireOp",EDGE,"E203.1.MirrorCS");var subQ61=sQuery(id+"F2.wireOp",EDGE,"E203.5.MirrorCS");var subQ62=sQuery(id+"F2.wireOp",EDGE,"E203.8.MirrorCS");var subQ70=sQuery(id+"F2.wireOp",EDGE,"E204.0.MirrorCS");var subQ71=sQuery(id+"F2.wireOp",EDGE,"E204.5.MirrorCS");var subQ75=sQuery(id+"F2.wireOp",EDGE,"E142");var subQ78=sQuery(id+"F2.wireOp",EDGE,"E147");var subQ79=makeQuery(id+"F2.imprint","INTERSECT",VERTEX,{"derivedFrom":[subQ75,subQ78]});var subQ81=makeQuery(id+"F2.imprint","IMPRINT",EDGE,{"disambiguationData":[TD([[subQ79,-1.0]])],"derivedFrom":subQ75});var subQ88=sQuery(id+"F2.wireOp",EDGE,"E145");var subQ90=sQuery(id+"F2.wireOp",EDGE,"E149");var subQ94=sQuery(id+"F2.wireOp",EDGE,"E143");var subQ97=sQuery(id+"F2.wireOp",EDGE,"E159");var subQ98=makeQuery(id+"F2.imprint","INTERSECT",VERTEX,{"derivedFrom":[subQ94,subQ97]});var subQ100=makeQuery(id+"F2.imprint","IMPRINT",EDGE,{"disambiguationData":[TD([[subQ98,-1.0]])],"derivedFrom":subQ94});var subQ106=sQuery(id+"F2.wireOp",EDGE,"E157");var subQ108=sQuery(id+"F2.wireOp",EDGE,"E161");var subQ112=sQuery(id+"F2.wireOp",EDGE,"E144");var subQ115=sQuery(id+"F2.wireOp",EDGE,"E171");var subQ116=makeQuery(id+"F2.imprint","INTERSECT",VERTEX,{"derivedFrom":[subQ112,subQ115]});var subQ118=makeQuery(id+"F2.imprint","IMPRINT",EDGE,{"disambiguationData":[TD([[subQ116,-1.0]])],"derivedFrom":subQ112});var subQ126=sQuery(id+"F2.wireOp",EDGE,"E169");var subQ128=sQuery(id+"F2.wireOp",EDGE,"E173");var subQ132=sQuery(id+"F2.wireOp",EDGE,"E181");var subQ135=sQuery(id+"F2.wireOp",EDGE,"E184");var subQ136=makeQuery(id+"F2.imprint","INTERSECT",VERTEX,{"derivedFrom":[subQ132,subQ135]});var subQ138=makeQuery(id+"F2.imprint","IMPRINT",EDGE,{"disambiguationData":[TD([[subQ136,-1.0]])],"derivedFrom":subQ132});var subQ146=sQuery(id+"F2.wireOp",EDGE,"E182");var subQ148=sQuery(id+"F2.wireOp",EDGE,"E186");var subQ152=sQuery(id+"F2.wireOp",EDGE,"E196");var subQ158=sQuery(id+"F2.wireOp",EDGE,"E205.0.MirrorCS");var subQ163=sQuery(id+"F2.wireOp",EDGE,"E205.1.MirrorCS");var subQ164=sQuery(id+"F2.wireOp",EDGE,"E205.3.MirrorCS");var subQ165=makeQuery(id+"F2.imprint","INTERSECT",VERTEX,{"derivedFrom":[subQ152,subQ164]});var subQ167=makeQuery(id+"F2.imprint","IMPRINT",EDGE,{"disambiguationData":[TD([[subQ165,1.0]])],"derivedFrom":subQ152});var subQ174=sQuery(id+"F2.wireOp",EDGE,"E206.2.MirrorCS");var subQ175=makeQuery(id+"F2.imprint","INTERSECT",VERTEX,{"derivedFrom":[subQ152,subQ174]});var subQ177=makeQuery(id+"F2.imprint","IMPRINT",EDGE,{"disambiguationData":[TD([[subQ175,-1.0]])],"derivedFrom":subQ152});var subQ185=sQuery(id+"F2.wireOp",EDGE,"E206.0.MirrorCS");var subQ187=sQuery(id+"F2.wireOp",EDGE,"E206.3.MirrorCS");Q0=qUnion([makeQuery(id+"F2.imprint","IMPRINT",FACE,{"disambiguationData":[TD([[makeQuery(id+"F2.imprint","IMPRINT",EDGE,{"derivedFrom":sQuery(id+"F2.wireOp",EDGE,"E151")}),1.0]])]}),makeQuery(id+"F2.imprint","IMPRINT",FACE,{"disambiguationData":[TD([[makeQuery(id+"F2.imprint","IMPRINT",EDGE,{"derivedFrom":subQ8}),1.0]])]}),makeQuery(id+"F2.imprint","IMPRINT",FACE,{"disambiguationData":[TD([[makeQuery(id+"F2.imprint","IMPRINT",EDGE,{"derivedFrom":subQ16}),-1.0]])]}),makeQuery(id+"F2.imprint","IMPRINT",FACE,{"disambiguationData":[TD([[makeQuery(id+"F2.imprint","IMPRINT",EDGE,{"derivedFrom":subQ17}),-1.0]])]}),makeQuery(id+"F2.imprint","IMPRINT",FACE,{"disambiguationData":[TD([[makeQuery(id+"F2.imprint","IMPRINT",EDGE,{"derivedFrom":subQ25}),-1.0]])]}),makeQuery(id+"F2.imprint","IMPRINT",FACE,{"disambiguationData":[TD([[makeQuery(id+"F2.imprint","IMPRINT",EDGE,{"derivedFrom":subQ26}),-1.0]])]}),makeQuery(id+"F2.imprint","IMPRINT",FACE,{"disambiguationData":[TD([[makeQuery(id+"F2.imprint","IMPRINT",EDGE,{"derivedFrom":subQ33}),-1.0]])]}),makeQuery(id+"F2.imprint","IMPRINT",FACE,{"disambiguationData":[TD([[makeQuery(id+"F2.imprint","IMPRINT",EDGE,{"derivedFrom":subQ35}),-1.0]])]}),makeQuery(id+"F2.imprint","IMPRINT",FACE,{"disambiguationData":[TD([[makeQuery(id+"F2.imprint","IMPRINT",EDGE,{"derivedFrom":subQ42}),1.0]])]}),makeQuery(id+"F2.imprint","IMPRINT",FACE,{"disambiguationData":[TD([[makeQuery(id+"F2.imprint","IMPRINT",EDGE,{"derivedFrom":sQuery(id+"F2.wireOp",EDGE,"E200.0.MirrorCS")}),-1.0]])]}),makeQuery(id+"F2.imprint","IMPRINT",FACE,{"disambiguationData":[TD([[makeQuery(id+"F2.imprint","IMPRINT",EDGE,{"derivedFrom":subQ52}),-1.0]])]}),makeQuery(id+"F2.imprint","IMPRINT",FACE,{"disambiguationData":[TD([[makeQuery(id+"F2.imprint","IMPRINT",EDGE,{"derivedFrom":subQ60}),1.0]])]}),makeQuery(id+"F2.imprint","IMPRINT",FACE,{"disambiguationData":[TD([[makeQuery(id+"F2.imprint","IMPRINT",EDGE,{"derivedFrom":subQ61}),1.0]])]}),makeQuery(id+"F2.imprint","IMPRINT",FACE,{"disambiguationData":[TD([[makeQuery(id+"F2.imprint","IMPRINT",EDGE,{"derivedFrom":subQ62}),-1.0]])]}),makeQuery(id+"F2.imprint","IMPRINT",FACE,{"disambiguationData":[TD([[makeQuery(id+"F2.imprint","IMPRINT",EDGE,{"derivedFrom":subQ70}),-1.0]])]}),makeQuery(id+"F2.imprint","IMPRINT",FACE,{"disambiguationData":[TD([[makeQuery(id+"F2.imprint","IMPRINT",EDGE,{"derivedFrom":subQ71}),-1.0]])]}),makeQuery(id+"F2.imprint","IMPRINT",FACE,{"disambiguationData":[TD([[subQ81,1.0]])]}),makeQuery(id+"F2.imprint","IMPRINT",FACE,{"disambiguationData":[TD([[subQ81,-1.0]])]}),makeQuery(id+"F2.imprint","IMPRINT",FACE,{"disambiguationData":[TD([[makeQuery(id+"F2.imprint","IMPRINT",EDGE,{"derivedFrom":subQ88}),1.0]])]}),makeQuery(id+"F2.imprint","IMPRINT",FACE,{"disambiguationData":[TD([[makeQuery(id+"F2.imprint","IMPRINT",EDGE,{"derivedFrom":subQ90}),1.0]])]}),makeQuery(id+"F2.imprint","IMPRINT",FACE,{"disambiguationData":[TD([[subQ100,1.0]])]}),makeQuery(id+"F2.imprint","IMPRINT",FACE,{"disambiguationData":[TD([[subQ100,-1.0]])]}),makeQuery(id+"F2.imprint","IMPRINT",FACE,{"disambiguationData":[TD([[makeQuery(id+"F2.imprint","IMPRINT",EDGE,{"derivedFrom":subQ106}),1.0]])]}),makeQuery(id+"F2.imprint","IMPRINT",FACE,{"disambiguationData":[TD([[makeQuery(id+"F2.imprint","IMPRINT",EDGE,{"derivedFrom":subQ108}),1.0]])]}),makeQuery(id+"F2.imprint","IMPRINT",FACE,{"disambiguationData":[TD([[subQ118,1.0]])]}),makeQuery(id+"F2.imprint","IMPRINT",FACE,{"disambiguationData":[TD([[subQ118,-1.0]])]}),makeQuery(id+"F2.imprint","IMPRINT",FACE,{"disambiguationData":[TD([[makeQuery(id+"F2.imprint","IMPRINT",EDGE,{"derivedFrom":subQ126}),1.0]])]}),makeQuery(id+"F2.imprint","IMPRINT",FACE,{"disambiguationData":[TD([[makeQuery(id+"F2.imprint","IMPRINT",EDGE,{"derivedFrom":subQ128}),1.0]])]}),makeQuery(id+"F2.imprint","IMPRINT",FACE,{"disambiguationData":[TD([[subQ138,1.0]])]}),makeQuery(id+"F2.imprint","IMPRINT",FACE,{"disambiguationData":[TD([[subQ138,-1.0]])]}),makeQuery(id+"F2.imprint","IMPRINT",FACE,{"disambiguationData":[TD([[makeQuery(id+"F2.imprint","IMPRINT",EDGE,{"derivedFrom":subQ146}),1.0]])]}),makeQuery(id+"F2.imprint","IMPRINT",FACE,{"disambiguationData":[TD([[makeQuery(id+"F2.imprint","IMPRINT",EDGE,{"derivedFrom":subQ148}),1.0]])]}),makeQuery(id+"F2.imprint","IMPRINT",FACE,{"disambiguationData":[TD([[makeQuery(id+"F2.imprint","IMPRINT",EDGE,{"derivedFrom":subQ158}),-1.0]])]}),makeQuery(id+"F2.imprint","IMPRINT",FACE,{"disambiguationData":[TD([[makeQuery(id+"F2.imprint","IMPRINT",EDGE,{"derivedFrom":subQ163}),-1.0]])]}),makeQuery(id+"F2.imprint","IMPRINT",FACE,{"disambiguationData":[TD([[subQ167,1.0]])]}),makeQuery(id+"F2.imprint","IMPRINT",FACE,{"disambiguationData":[TD([[subQ167,-1.0]])]}),makeQuery(id+"F2.imprint","IMPRINT",FACE,{"disambiguationData":[TD([[subQ177,1.0]])]}),makeQuery(id+"F2.imprint","IMPRINT",FACE,{"disambiguationData":[TD([[subQ177,-1.0]])]}),makeQuery(id+"F2.imprint","IMPRINT",FACE,{"disambiguationData":[TD([[makeQuery(id+"F2.imprint","IMPRINT",EDGE,{"derivedFrom":subQ185}),1.0]])]}),makeQuery(id+"F2.imprint","IMPRINT",FACE,{"disambiguationData":[TD([[makeQuery(id+"F2.imprint","IMPRINT",EDGE,{"derivedFrom":subQ187}),1.0]])]})]);}
            extrude(context, id + "F3", {"entities" : qUnion([Q0]), "operationType" : NewBodyOperationType.REMOVE, "oppositeDirection" : true, "depth" : 1200 * mm});
        }
        {
            var Q0;
            Q0=makeQuery(id+"F1.opExtrude","SWEPT_EDGE",EDGE,{"disambiguationData":[OSD([sQuery(id+"F0.wireOp",EDGE,"E19.bottom"),sQuery(id+"F0.wireOp",EDGE,"E20.left")])]});
            var Q1;
            Q1=makeQuery(id+"F1.opExtrude","SWEPT_EDGE",EDGE,{"disambiguationData":[OSD([sQuery(id+"F0.wireOp",EDGE,"E0"),sQuery(id+"F0.wireOp",EDGE,"E16.bottom")])]});
            var Q2;
            Q2=makeQuery(id+"F1.opExtrude","SWEPT_EDGE",EDGE,{"disambiguationData":[OSD([sQuery(id+"F0.wireOp",EDGE,"E0"),sQuery(id+"F0.wireOp",EDGE,"E17.bottom")])]});
            var Q3;
            Q3=makeQuery(id+"F1.opExtrude","SWEPT_EDGE",EDGE,{"disambiguationData":[OSD([sQuery(id+"F0.wireOp",EDGE,"E17.bottom"),sQuery(id+"F0.wireOp",EDGE,"E20.left")])]});
            var Q4;
            Q4=makeQuery(id+"F1.opExtrude","SWEPT_EDGE",EDGE,{"disambiguationData":[OSD([sQuery(id+"F0.wireOp",EDGE,"E18.left"),sQuery(id+"F0.wireOp",EDGE,"E19.bottom")])]});
            var Q5;
            Q5=makeQuery(id+"F1.opExtrude","SWEPT_EDGE",EDGE,{"disambiguationData":[OSD([sQuery(id+"F0.wireOp",EDGE,"E2"),sQuery(id+"F0.wireOp",EDGE,"E16.bottom")])]});
            fillet(context, id + "F4", {"entities" : qUnion([Q0, Q1, Q2, Q3, Q4, Q5]), "radius" : 2 * mm, "tangentPropagation" : true, "allowEdgeOverflow" : false});
        }
        {
            var Q0;
            Q0=makeQuery(id+"F1.opExtrude","SWEPT_EDGE",EDGE,{"disambiguationData":[OSD([sQuery(id+"F0.wireOp",EDGE,"E27.2"),sQuery(id+"F0.wireOp",EDGE,"E27.3")])]});
            var Q1;
            Q1=makeQuery(id+"F1.opExtrude","SWEPT_EDGE",EDGE,{"disambiguationData":[OSD([sQuery(id+"F0.wireOp",EDGE,"E26.2"),sQuery(id+"F0.wireOp",EDGE,"E26.3")])]});
            chamfer(context, id + "F5", {"entities" : qUnion([Q0, Q1]), "width" : 1 * mm, "tangentPropagation" : true});
        }
    });
